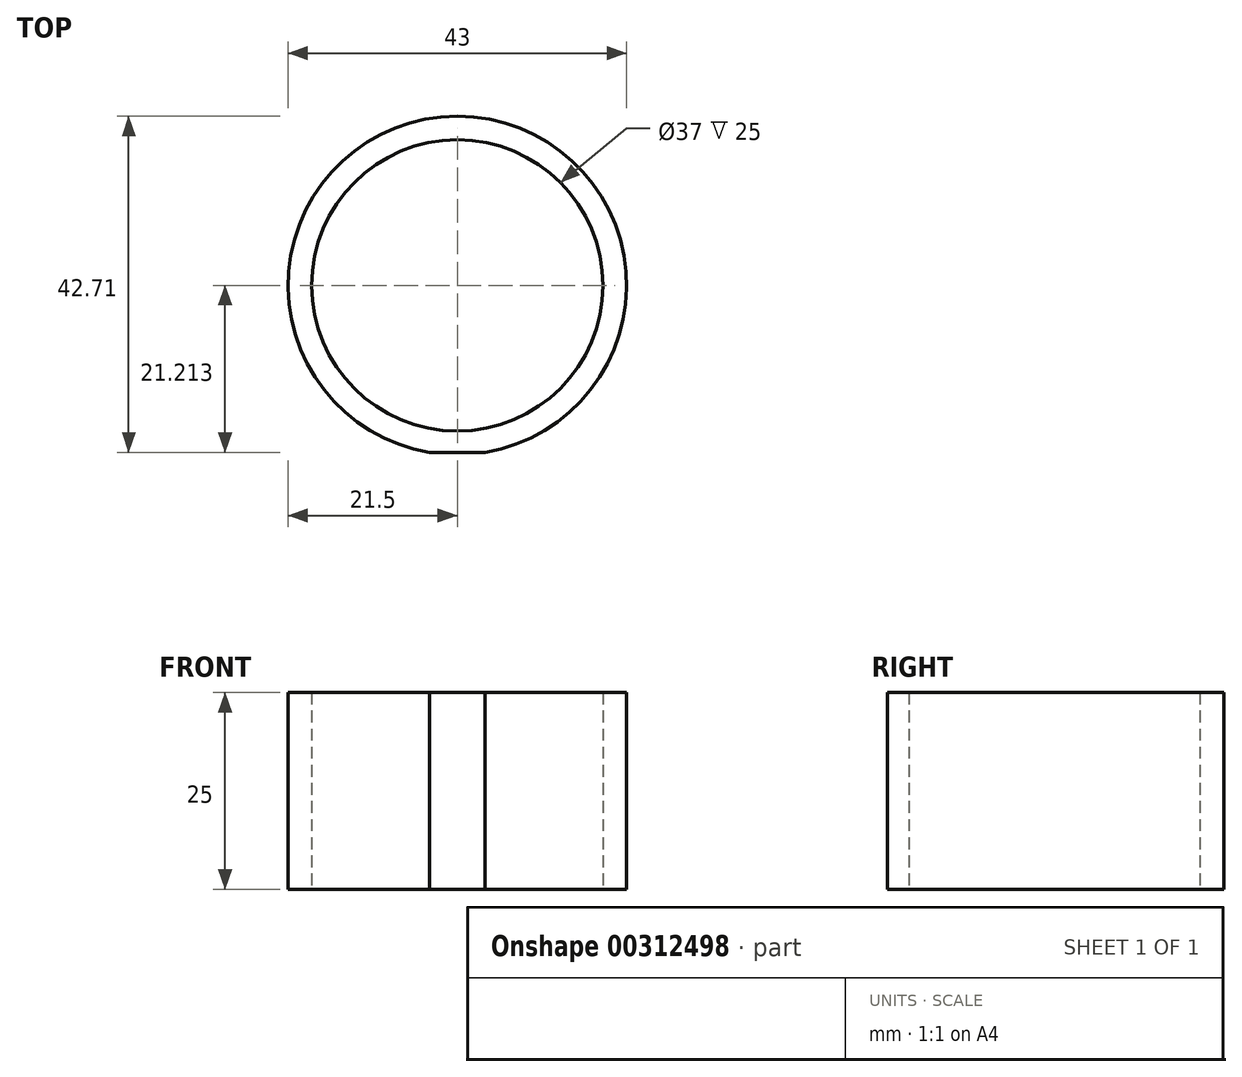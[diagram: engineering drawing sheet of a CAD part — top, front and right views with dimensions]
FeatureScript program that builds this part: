
annotation { "Feature Type Name" : "Feature", "Feature Type Description" : "" }
export const myFeature = defineFeature(function(context is Context, id is Id, definition is map)
    precondition{}
    {
        {
            var Q0;
            Q0=qCreatedBy(makeId("Top.planeOp"),FACE);
            var sketch = newSketch(context, id + "F0", { "sketchPlane" : qUnion([Q0])});
            skLineSegment(sketch, "E0.bottom", {"start": v(0, 0) * mm, "end": v(7, 0) * mm});
            skLineSegment(sketch, "E0.top", {"start": v(0, -10) * mm, "end": v(7, -10) * mm});
            skLineSegment(sketch, "E0.left", {"start": v(0, 0) * mm, "end": v(0, -10) * mm});
            skLineSegment(sketch, "E0.right", {"start": v(7, 0) * mm, "end": v(7, -10) * mm});
            skArc(sketch, "E1", {"start": v(7, 0) * mm, "mid": v(3.5, 42.71) * mm, "end": v(0, 0) * mm});
            skCircle(sketch, "E2", {"center": v(3.5, 21.21) * mm, "radius": 18.5 * mm});
            skSolve(sketch);
        }
        {
            var Q0;
            Q0=makeQuery(id+"F0.imprint","IMPRINT",FACE,{"disambiguationData":[TD([[makeQuery(id+"F0.imprint","IMPRINT",EDGE,{"derivedFrom":sQuery(id+"F0.wireOp",EDGE,"E0.bottom")}),1.0]])]});
            extrude(context, id + "F1", {"entities" : qUnion([Q0]), "depth" : 25 * mm});
        }
    });
